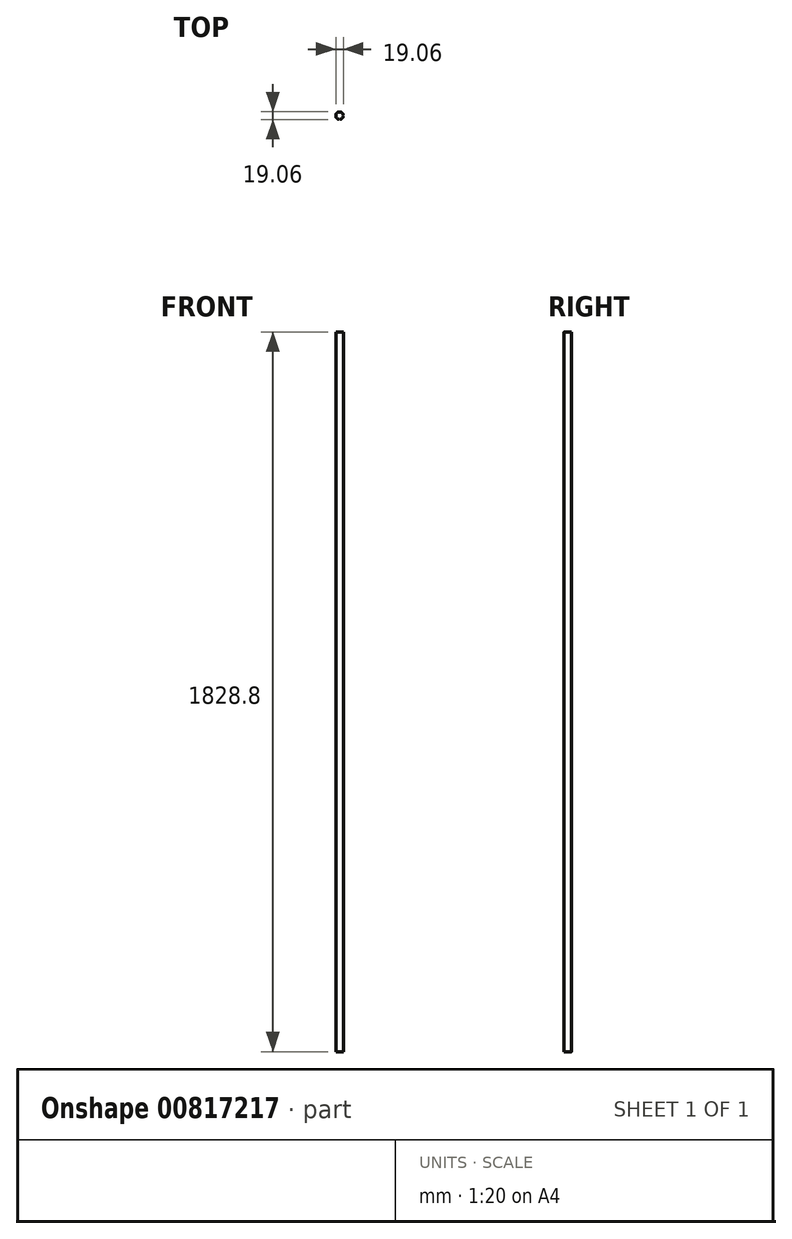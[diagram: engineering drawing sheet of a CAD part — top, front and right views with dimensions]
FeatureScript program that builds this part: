
annotation { "Feature Type Name" : "Feature", "Feature Type Description" : "" }
export const myFeature = defineFeature(function(context is Context, id is Id, definition is map)
    precondition{}
    {
        {
            var Q0;
            Q0=qCreatedBy(makeId("Top.planeOp"),FACE);
            var sketch = newSketch(context, id + "F0", { "sketchPlane" : qUnion([Q0])});
            skCircle(sketch, "E0", {"center": v(0, 0) * mm, "radius": 9.53 * mm});
            skSolve(sketch);
        }
        {
            var Q0;
            Q0=sQuery(id+"F0.wireOp",EDGE,"E0");
            extrude(context, id + "F1", {"bodyType" : ToolBodyType.SURFACE, "surfaceEntities" : qUnion([Q0]), "depth" : 1828.8 * mm, "offsetDistance" : 25.4 * mm});
        }
    });
